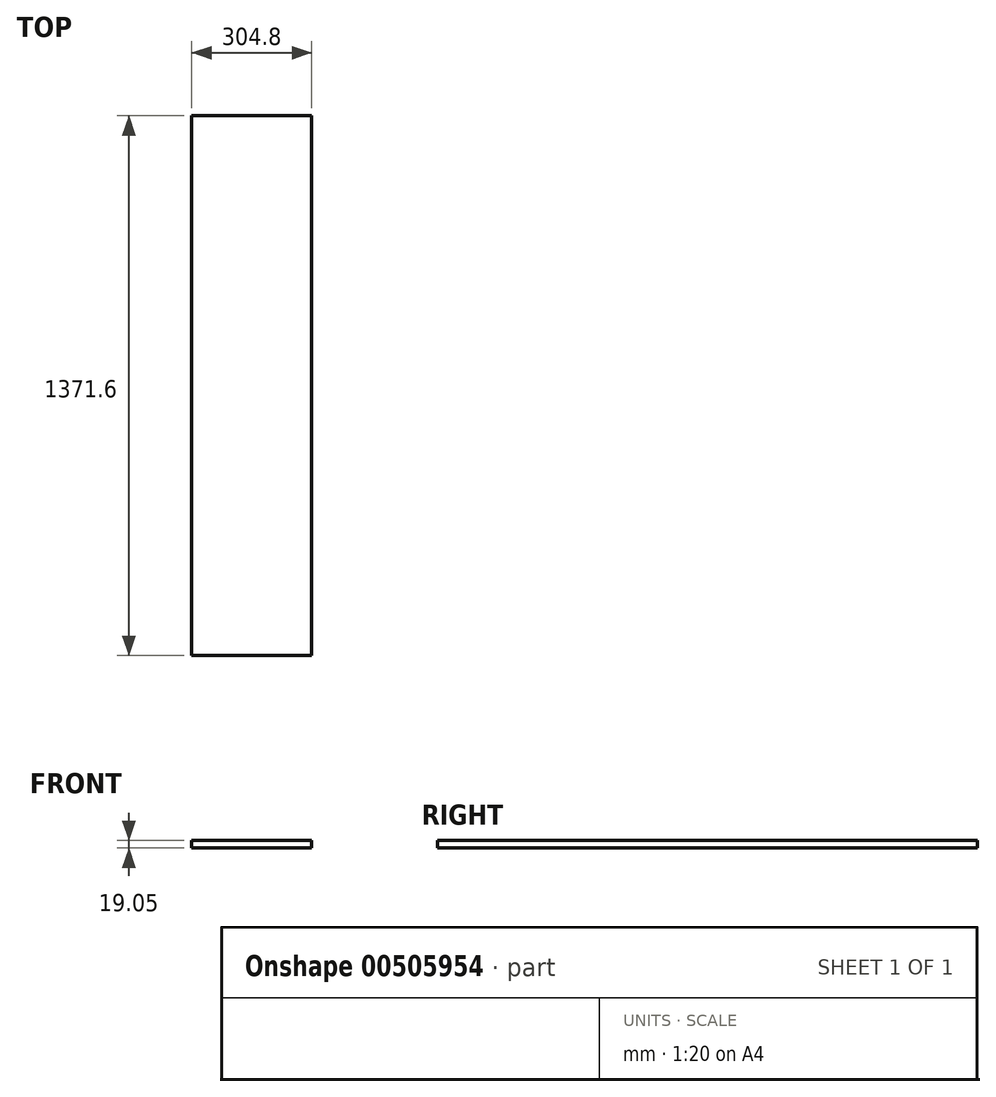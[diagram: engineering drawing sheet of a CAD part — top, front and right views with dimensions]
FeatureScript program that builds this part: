
annotation { "Feature Type Name" : "Feature", "Feature Type Description" : "" }
export const myFeature = defineFeature(function(context is Context, id is Id, definition is map)
    precondition{}
    {
        {
            var Q0;
            Q0=qCreatedBy(makeId("Top.planeOp"),FACE);
            var sketch = newSketch(context, id + "F0", { "sketchPlane" : qUnion([Q0])});
            skLineSegment(sketch, "E0.bottom", {"start": v(-39.06, 1304.51) * mm, "end": v(265.74, 1304.51) * mm});
            skLineSegment(sketch, "E0.top", {"start": v(-39.06, -67.09) * mm, "end": v(265.74, -67.09) * mm});
            skLineSegment(sketch, "E0.left", {"start": v(-39.06, 1304.51) * mm, "end": v(-39.06, -67.09) * mm});
            skLineSegment(sketch, "E0.right", {"start": v(265.74, 1304.51) * mm, "end": v(265.74, -67.09) * mm});
            skSolve(sketch);
        }
        {
            var Q0;
            Q0=makeQuery(id+"F0.imprint","IMPRINT",FACE,{"disambiguationData":[TD([[makeQuery(id+"F0.imprint","IMPRINT",EDGE,{"derivedFrom":sQuery(id+"F0.wireOp",EDGE,"E0.bottom")}),-1.0]])]});
            extrude(context, id + "F1", {"entities" : qUnion([Q0]), "depth" : 19.05 * mm, "offsetDistance" : 25.4 * mm});
        }
    });
